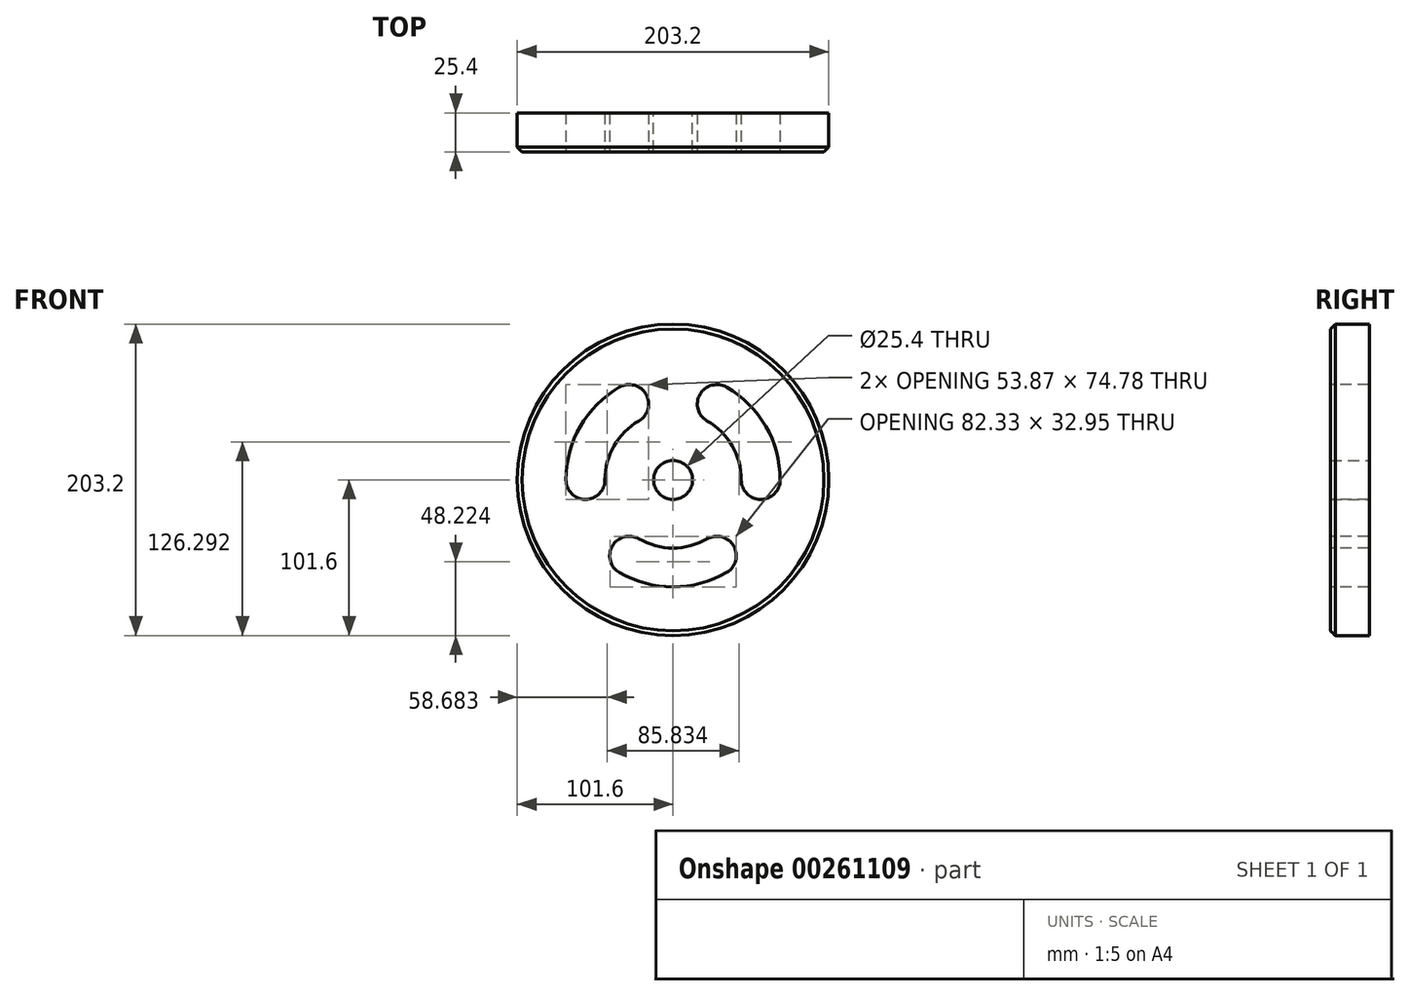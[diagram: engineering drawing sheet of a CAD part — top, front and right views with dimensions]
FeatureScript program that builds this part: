
annotation { "Feature Type Name" : "Feature", "Feature Type Description" : "" }
export const myFeature = defineFeature(function(context is Context, id is Id, definition is map)
    precondition{}
    {
        {
            var Q0;
            Q0=qCreatedBy(makeId("Front.planeOp"),FACE);
            var sketch = newSketch(context, id + "F0", { "sketchPlane" : qUnion([Q0])});
            skCircle(sketch, "E0", {"center": v(0, 0) * mm, "radius": 101.6 * mm});
            skSolve(sketch);
        }
        {
            var Q0;
            Q0=qCreatedBy(makeId("Front.planeOp"),FACE);
            var sketch = newSketch(context, id + "F1", { "sketchPlane" : qUnion([Q0])});
            skCircle(sketch, "E1", {"center": v(0, 0) * mm, "radius": 12.7 * mm});
            skSolve(sketch);
        }
        {
            var Q0;
            Q0 = qSketchRegion(id + "F0", true);
            extrude(context, id + "F2", {"entities" : qUnion([Q0]), "depth" : 25.4 * mm});
        }
        {
            var Q0;
            Q0 = qSketchRegion(id + "F1", true);
            extrude(context, id + "F3", {"entities" : qUnion([Q0]), "operationType" : NewBodyOperationType.REMOVE, "endBound" : BoundingType.THROUGH_ALL, "depth" : 25.4 * mm});
        }
        {
            var Q0;
            Q0=makeQuery(id+"F2.opExtrude","CAP_FACE",FACE,{"disambiguationData":[OSD([sQuery(id+"F0.wireOp",EDGE,"E0")])],"isStart":false});
            var sketch = newSketch(context, id + "F4", { "sketchPlane" : qUnion([Q0])});
            skArc(sketch, "E2", {"start": v(44.45, 0) * mm, "mid": v(57.15, -12.7) * mm, "end": v(69.85, 0) * mm});
            skArc(sketch, "E3", {"start": v(34.93, 60.5) * mm, "mid": v(17.58, 55.84) * mm, "end": v(22.23, 38.5) * mm});
            skLineSegment(sketch, "E4", {"start": v(44.45, 0) * mm, "end": v(44.45, 0) * mm});
            skCircle(sketch, "E5", {"center": v(0, 0) * mm, "radius": 57.15 * mm, "construction": true});
            skArc(sketch, "E6", {"start": v(44.45, 0) * mm, "mid": v(38.5, 22.22) * mm, "end": v(22.23, 38.5) * mm});
            skArc(sketch, "E7", {"start": v(69.85, 0) * mm, "mid": v(60.5, 34.92) * mm, "end": v(34.93, 60.5) * mm});
            skLineSegment(sketch, "E8", {"start": v(0, 0) * mm, "end": v(28.58, 49.5) * mm, "construction": true});
            skLineSegment(sketch, "E9", {"start": v(0, 0) * mm, "end": v(123.3, 0) * mm, "construction": true});
            skArc(sketch, "E10.1.0", {"start": v(-22.22, 38.5) * mm, "mid": v(-38.5, 22.23) * mm, "end": v(-44.45, 0) * mm});
            skArc(sketch, "E10.1.1", {"start": v(-22.22, 38.5) * mm, "mid": v(-17.58, 55.84) * mm, "end": v(-34.92, 60.5) * mm});
            skArc(sketch, "E10.1.2", {"start": v(-34.92, 60.5) * mm, "mid": v(-60.5, 34.93) * mm, "end": v(-69.85, 0) * mm});
            skArc(sketch, "E10.1.3", {"start": v(-69.85, 0) * mm, "mid": v(-57.15, -12.7) * mm, "end": v(-44.45, 0) * mm});
            skArc(sketch, "E10.2.0", {"start": v(-22.23, -38.5) * mm, "mid": v(0, -44.45) * mm, "end": v(22.22, -38.5) * mm});
            skArc(sketch, "E10.2.1", {"start": v(-22.23, -38.5) * mm, "mid": v(-39.57, -43.14) * mm, "end": v(-34.93, -60.5) * mm});
            skArc(sketch, "E10.2.2", {"start": v(-34.93, -60.5) * mm, "mid": v(0, -69.85) * mm, "end": v(34.92, -60.5) * mm});
            skArc(sketch, "E10.2.3", {"start": v(34.92, -60.5) * mm, "mid": v(39.57, -43.14) * mm, "end": v(22.22, -38.5) * mm});
            skSolve(sketch);
        }
        {
            var Q0;
            Q0 = qSketchRegion(id + "F4", true);
            extrude(context, id + "F5", {"entities" : qUnion([Q0]), "operationType" : NewBodyOperationType.REMOVE, "endBound" : BoundingType.THROUGH_ALL, "oppositeDirection" : true, "depth" : 25.4 * mm});
        }
        {
            var Q0;
            Q0=makeQuery(id+"F2.opExtrude","CAP_EDGE",EDGE,{"disambiguationData":[OSD([sQuery(id+"F0.wireOp",EDGE,"E0")])],"isStart":false});
            var Q1;
            Q1=makeQuery(id+"F5.boolean.opBoolean","COPY",EDGE,{"derivedFrom":makeQuery(id+"F5.opExtrude","CAP_EDGE",EDGE,{"disambiguationData":[OSD([sQuery(id+"F4.wireOp",EDGE,"E10.1.2")])],"isStart":true})});
            var Q2;
            Q2=makeQuery(id+"F5.boolean.opBoolean","COPY",EDGE,{"derivedFrom":makeQuery(id+"F5.opExtrude","CAP_EDGE",EDGE,{"disambiguationData":[OSD([sQuery(id+"F4.wireOp",EDGE,"E6")])],"isStart":true})});
            var Q3;
            Q3=makeQuery(id+"F5.boolean.opBoolean","COPY",EDGE,{"derivedFrom":makeQuery(id+"F5.opExtrude","CAP_EDGE",EDGE,{"disambiguationData":[OSD([sQuery(id+"F4.wireOp",EDGE,"E10.2.0")])],"isStart":true})});
            chamfer(context, id + "F6", {"entities" : qUnion([Q0, Q1, Q2, Q3]), "width" : 3.17 * mm, "tangentPropagation" : true});
        }
    });
